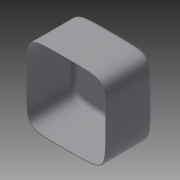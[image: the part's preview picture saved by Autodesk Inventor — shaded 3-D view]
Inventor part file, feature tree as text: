
AUTODESK INVENTOR PART (.ipt)
format: ipt  version: 2014 SP1 (Build 180222100, 222)  size: 287,744 bytes
history: native  units: in
note: dims shown in document units (in); Inventor stores cm internally (conversion verified against a paired STEP export)
features: extrude x1, fillet x1, shell x1, sketch x1
ambient origin geometry x8: Origin, YZ Plane, XZ Plane, XY Plane, X Axis, Y Axis, Z Axis, Center Point
bodies: Solid1 (feature_tree)
feature tree (4):
  extrude  "Extrusion1"  Depth=3.0in
  fillet  "Fillet1"  Radius=3.0in
  shell  "Shell1"  Thickness=4.5in
  sketch  "Sketch1"  dims[d2=0.25in d12=3.0in d13=3.0in d18=4.5in d19=0.0in d20=0.5in d21=0.0625in]
